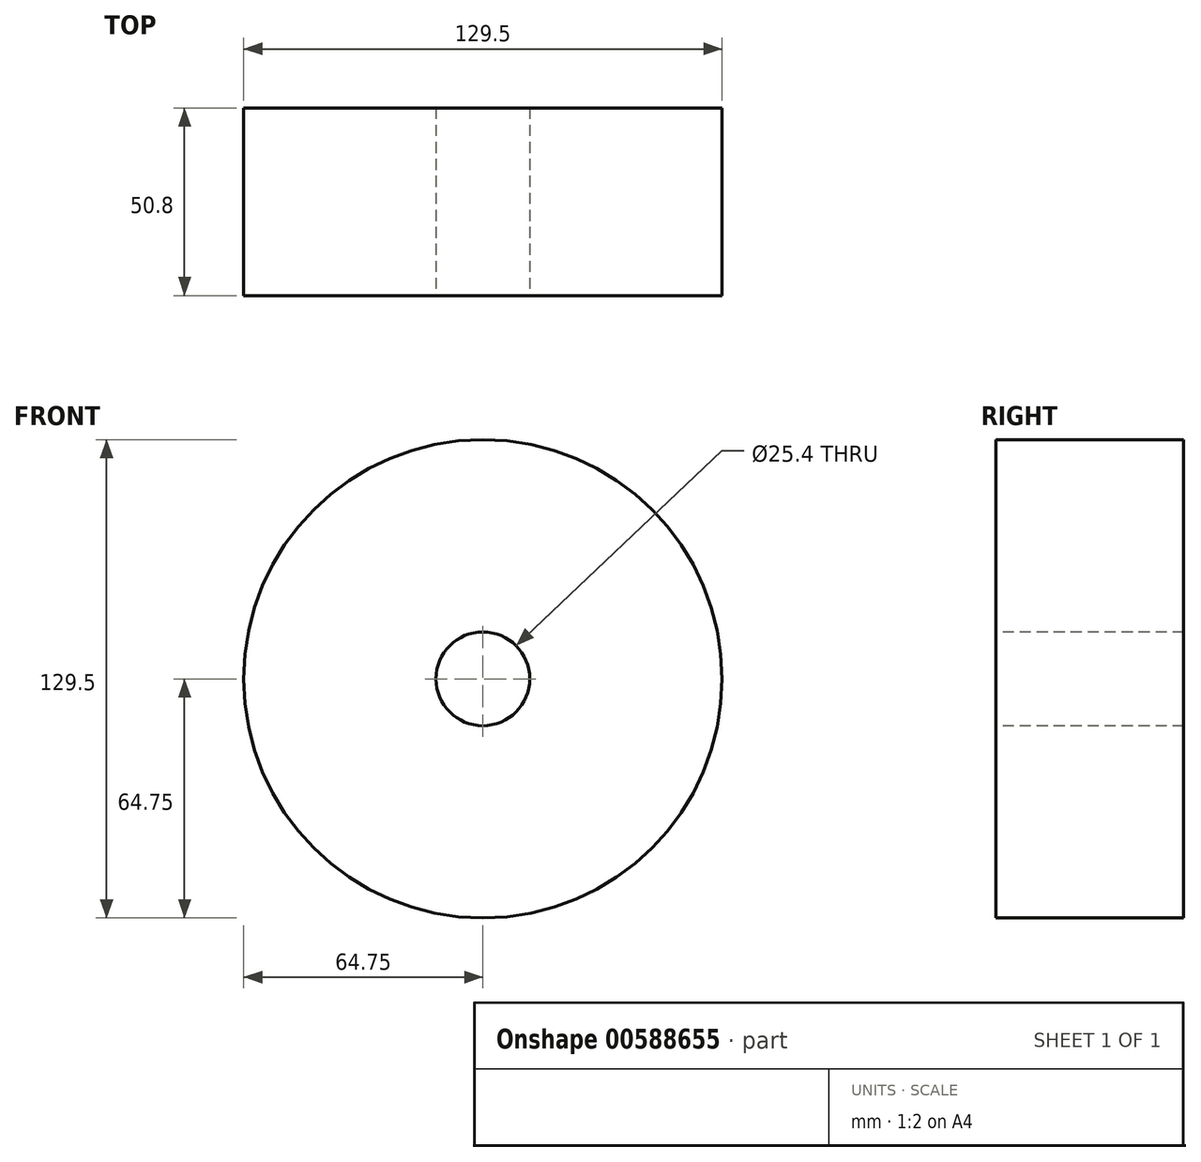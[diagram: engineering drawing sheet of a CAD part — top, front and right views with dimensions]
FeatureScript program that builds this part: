
annotation { "Feature Type Name" : "Feature", "Feature Type Description" : "" }
export const myFeature = defineFeature(function(context is Context, id is Id, definition is map)
    precondition{}
    {
        {
            var Q0;
            Q0=qCreatedBy(makeId("Front.planeOp"),FACE);
            var sketch = newSketch(context, id + "F0", { "sketchPlane" : qUnion([Q0])});
            skCircle(sketch, "E0", {"center": v(0, 0) * mm, "radius": 64.75 * mm});
            skSolve(sketch);
        }
        {
            var Q0;
            Q0=makeQuery(id+"F0.imprint","IMPRINT",FACE,{"disambiguationData":[TD([[makeQuery(id+"F0.imprint","IMPRINT",EDGE,{"derivedFrom":sQuery(id+"F0.wireOp",EDGE,"E0")}),1.0]])]});
            var Q1;
            Q1 = qSketchRegion(id + "F0", true);
            extrude(context, id + "F1", {"entities" : qUnion([Q0, Q1]), "depth" : 50.8 * mm, "offsetDistance" : 25.4 * mm});
        }
        {
            var Q0;
            Q0=makeQuery(id+"F1.opExtrude","CAP_FACE",FACE,{"disambiguationData":[OSD([sQuery(id+"F0.wireOp",EDGE,"E0")])],"isStart":false});
            var sketch = newSketch(context, id + "F2", { "sketchPlane" : qUnion([Q0])});
            skCircle(sketch, "E1", {"center": v(0, 0) * mm, "radius": 38.9 * mm});
            skSolve(sketch);
        }
        {
            var Q0;
            Q0=sQuery(id+"F2.wireOp",VERTEX,"E1.center");
            var Q1;
            Q1=makeQuery(id+"F1.opExtrude","SWEPT_BODY",BODY,{"disambiguationData":[OSD([sQuery(id+"F0.wireOp",EDGE,"E0")])]});
            hole(context, id + "F3", {"style" : HoleStyle.SIMPLE, "endStyle" : HoleEndStyle.THROUGH, "holeDiameter" : 25.4 * mm, "majorDiameter" : 6.35 * mm, "isTappedThrough" : true, "tappedDepth" : 12.7 * mm, "tapClearance" : 3, "locations" : qUnion([Q0]), "scope" : qUnion([Q1])});
        }
    });
